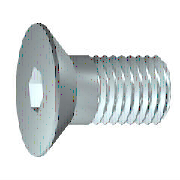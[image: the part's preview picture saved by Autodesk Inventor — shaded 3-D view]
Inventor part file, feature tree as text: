
AUTODESK INVENTOR PART (.ipt)
format: ipt  version: 2020 (Build 240168000, 168)  size: 186,368 bytes
history: native  units: mm (DEFAULTED — no unit token found)
features: other x4, sketch x3, fillet x1, chamfer x1
ambient origin geometry x8: Origin, YZ Plane, XZ Plane, XY Plane, X Axis, Y Axis, Z Axis, Center Point
bodies: Solid1 (feature_tree)
feature tree (9):
  sketch  "Sketch1"  dims[d2=3.0mm]
  other  "WorkPoint1"
  sketch  "Sketch2"  dims[d3=4.0mm]
  fillet  "Fillet1"  [1 undecoded]
  chamfer  "Chamfer1"  Distance=2.0mm
  other  "MSC_A1"
  other  "MSC_PF1"
  other  "MSC_PT1"
  sketch  "Sketch3"  dims[d4=1.5mm d5=2.0mm d6=8.0mm d7=40.0mm d8=360.0deg d9=0.0mm d10=2.0mm d11=2.5mm d12=120.0deg d13=120.0deg d14=120.0deg d15=120.0deg d16=1.8mm d17=0.0mm d18=0.2mm d19=0.35mm d20=45.0deg d22=0.0mm d23=0.0mm d35=0.0mm d37=0.0mm d38=0.0mm d39=0.35mm d40=0.0mm d41=0.0mm d42=0.0mm d43=45.0deg]
note: 1 required parameter value undecoded (feature->parameter linkage not recoverable at this tier; creation-order binding heuristic only, values carry confidence <= 0.55)
